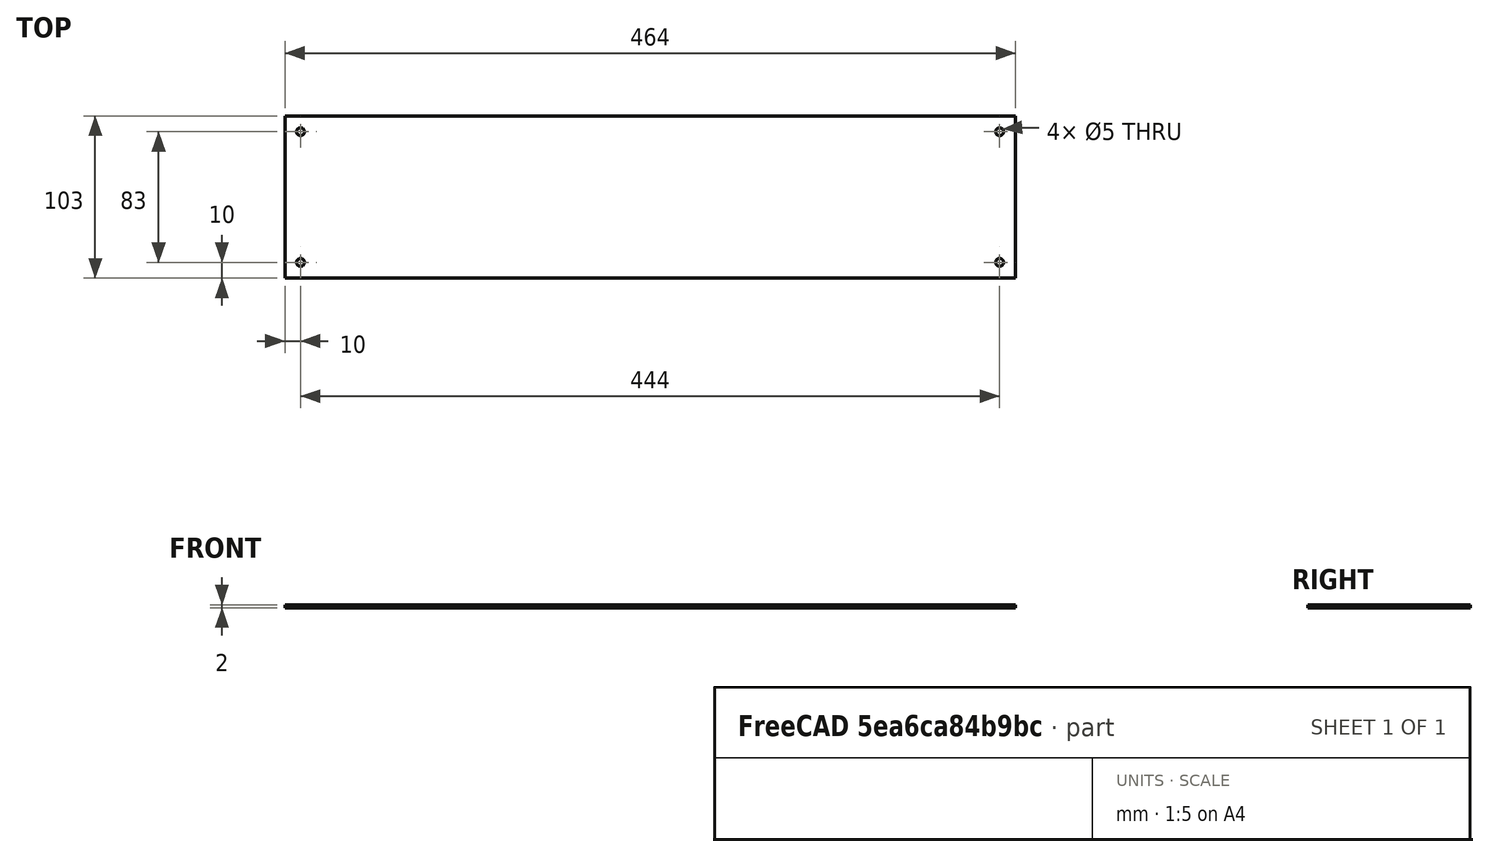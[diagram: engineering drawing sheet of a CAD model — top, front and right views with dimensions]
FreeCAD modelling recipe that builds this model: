
FCSTD DOCUMENT  (FreeCAD 0.16R6698 (Git))
Label: Plaque_access_PSU
License: All rights reserved
LicenseURL: http://en.wikipedia.org/wiki/All_rights_reserved
objects: Sketcher::SketchObject×1, PartDesign::Pad×1
note: 3 computed .brp shape members not serialized (recipe doc carries the construction recipe); baked Part::Feature solids carry a one-line shape summary decoded from their .brp

FEATURE [Sketcher::SketchObject] Sketch
  sketch-geometry (8):
    g0: LineSegment StartX=-232 StartY=51.5 StartZ=0 EndX=232 EndY=51.5 EndZ=0
    g1: LineSegment StartX=232 StartY=51.5 StartZ=0 EndX=232 EndY=-51.5 EndZ=0
    g2: LineSegment StartX=232 StartY=-51.5 StartZ=0 EndX=-232 EndY=-51.5 EndZ=0
    g3: LineSegment StartX=-232 StartY=-51.5 StartZ=0 EndX=-232 EndY=51.5 EndZ=0
    g4: Circle CenterX=-222 CenterY=41.5 CenterZ=0 NormalX=0 NormalY=0 NormalZ=1 Radius=2.5
    g5: Circle CenterX=-222 CenterY=-41.5 CenterZ=0 NormalX=0 NormalY=0 NormalZ=1 Radius=2.5
    g6: Circle CenterX=222 CenterY=-41.5 CenterZ=0 NormalX=0 NormalY=0 NormalZ=1 Radius=2.5
    g7: Circle CenterX=222 CenterY=41.5 CenterZ=0 NormalX=0 NormalY=0 NormalZ=1 Radius=2.5
  constraints (24):
    c: Coincident(g0,g1)
    c: Coincident(g1,g2)
    c: Coincident(g2,g3)
    c: Coincident(g3,g0)
    c: Horizontal(g0)
    c: Horizontal(g2)
    c: Vertical(g1)
    c: Vertical(g3)
    c: DistanceX(g0,g0) = 464
    c: DistanceY(g1,g1) = 103
    c: Radius(g7) = 2.5
    c: Equal(g7,g6)
    c: Equal(g7,g5)
    c: Equal(g7,g4)
    c: DistanceY(g4,g0) = 10
    c: DistanceX(g0,g4) = 10
    c: DistanceY(g2,g5) = 10
    c: DistanceX(g2,g5) = 10
    c: DistanceY(g1,g6) = 10
    c: DistanceX(g6,g1) = 10
    c: DistanceX(g7,g0) = 10
    c: DistanceY(g7,g0) = 10
    c: DistanceX(g-1,g0) = 232
    c: DistanceY(g-1,g0) = 51.5
FEATURE [PartDesign::Pad] Pad
  Length = 2
  Length2 = 100
  Sketch = -> Sketch
  Type = 0
